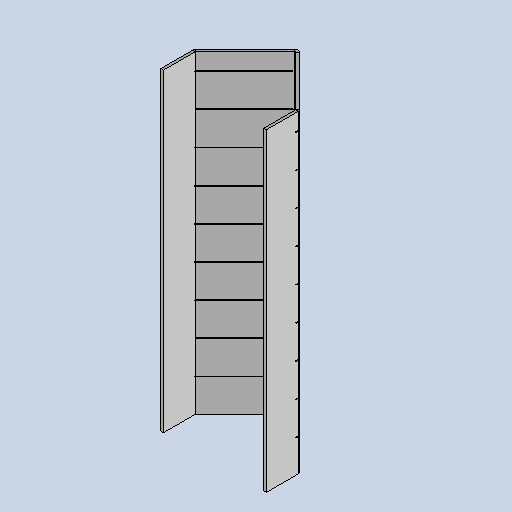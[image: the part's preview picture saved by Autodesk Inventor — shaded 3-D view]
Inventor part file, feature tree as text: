
AUTODESK INVENTOR PART (.ipt)
format: ipt  version: 2025.3 (Build 293356030, 356C)  size: 438,784 bytes
history: native  units: mm
features: sheet_metal_op x3, sketch x3, other x3, mirror x1
ambient origin geometry x8: Origin, YZ Plane, XZ Plane, XY Plane, X Axis, Y Axis, Z Axis, Center Point
bodies: Body1 (feature_tree)
feature tree (10):
  sheet_metal_op  "Contour Flange1"
  mirror  "Mirror2"
  sketch  "Sketch3"  dims[d15=10.0mm]
  other  "Plate1"
  sheet_metal_op  "Bend1"
  sheet_metal_op  "Corner1"
  sketch  "Sketch5"  dims[d19=1.0mm d20=1.0mm d21=0.8mm d22=0.8mm d23=0.4mm d24=1.6mm d25=0.8mm d26=95.0mm d27=0.8mm d28=0.8mm d29=3.2mm d30=0.8mm d31=0.8mm d32=32.0mm d33=90.0deg d111=0.2mm d112=28.0mm d113=5.0mm d114=0.5mm d115=90.0mm d116=10.0mm d73=10.0mm d75=10.0mm d97=5.0mm d98=0.8mm d99=0.0mm d101=0.5mm d102=0.872665mm d103=0.5mm d104=0.872665mm]
  sketch  "Sketch Rectangular Pattern3"  dims[d18=1.0mm]
  other  "Cut3"
  other  "Definition1"
